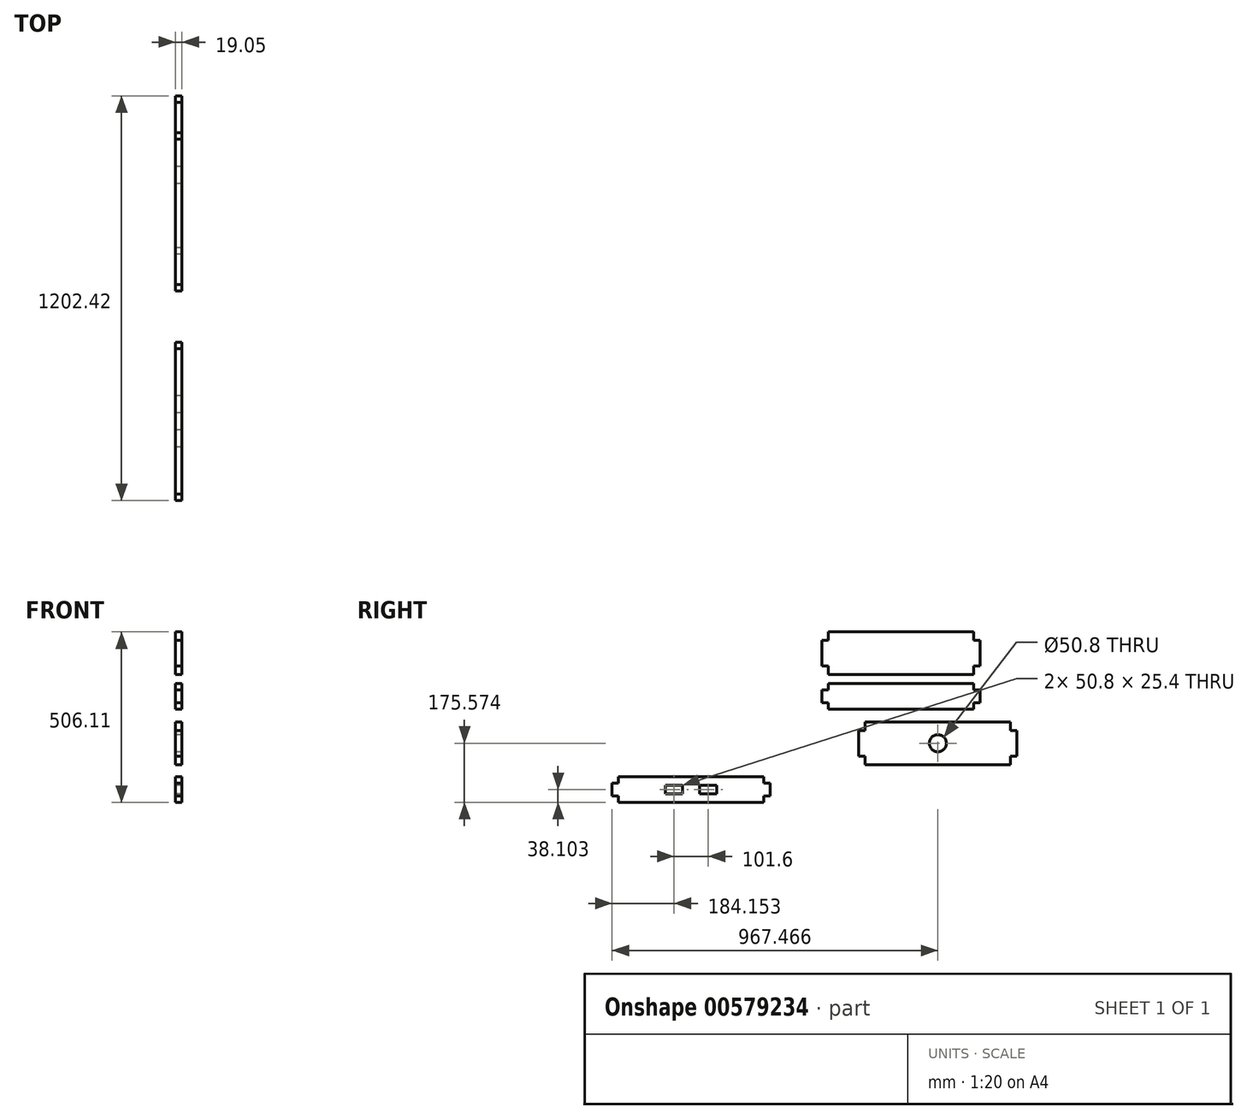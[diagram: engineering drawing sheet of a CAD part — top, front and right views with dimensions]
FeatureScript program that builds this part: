
annotation { "Feature Type Name" : "Feature", "Feature Type Description" : "" }
export const myFeature = defineFeature(function(context is Context, id is Id, definition is map)
    precondition{}
    {
        {
            var Q0;
            Q0=qCreatedBy(makeId("Right.planeOp"),FACE);
            var sketch = newSketch(context, id + "F0", { "sketchPlane" : qUnion([Q0])});
            skLineSegment(sketch, "E0.bottom", {"start": v(-63.54, 0) * mm, "end": v(368.26, 0) * mm});
            skLineSegment(sketch, "E0.top", {"start": v(-63.54, 76.2) * mm, "end": v(368.26, 76.2) * mm});
            skLineSegment(sketch, "E0.left", {"start": v(-63.54, 0) * mm, "end": v(-63.54, 19.05) * mm});
            skLineSegment(sketch, "E0.right", {"start": v(368.26, 0) * mm, "end": v(368.26, 19.05) * mm});
            skLineSegment(sketch, "E1.bottom", {"start": v(-63.54, 57.15) * mm, "end": v(-82.6, 57.15) * mm});
            skLineSegment(sketch, "E1.top", {"start": v(-63.54, 19.05) * mm, "end": v(-82.6, 19.05) * mm});
            skLineSegment(sketch, "E1.right", {"start": v(-82.6, 57.15) * mm, "end": v(-82.6, 19.05) * mm});
            skLineSegment(sketch, "E2.bottom", {"start": v(387.3, 57.15) * mm, "end": v(368.26, 57.15) * mm});
            skLineSegment(sketch, "E2.top", {"start": v(387.3, 19.05) * mm, "end": v(368.26, 19.05) * mm});
            skLineSegment(sketch, "E2.left", {"start": v(387.3, 57.15) * mm, "end": v(387.3, 19.05) * mm});
            skLineSegment(sketch, "E3.trimOffspring", {"start": v(-63.54, 57.15) * mm, "end": v(-63.54, 76.2) * mm});
            skLineSegment(sketch, "E4.trimOffspring", {"start": v(368.26, 57.15) * mm, "end": v(368.26, 76.2) * mm});
            skLineSegment(sketch, "E5.bottom", {"start": v(368.26, 102.68) * mm, "end": v(-63.54, 102.68) * mm});
            skLineSegment(sketch, "E5.top", {"start": v(368.26, 229.68) * mm, "end": v(-63.54, 229.68) * mm});
            skLineSegment(sketch, "E5.left", {"start": v(368.26, 102.68) * mm, "end": v(368.26, 128.08) * mm});
            skLineSegment(sketch, "E5.right", {"start": v(-63.54, 102.68) * mm, "end": v(-63.54, 128.08) * mm});
            skLineSegment(sketch, "E6", {"start": v(368.26, 229.68) * mm, "end": v(368.26, 204.28) * mm});
            skLineSegment(sketch, "E7", {"start": v(387.3, 204.28) * mm, "end": v(368.26, 204.28) * mm});
            skLineSegment(sketch, "E8", {"start": v(387.3, 204.28) * mm, "end": v(387.3, 128.08) * mm});
            skLineSegment(sketch, "E9", {"start": v(368.26, 128.08) * mm, "end": v(387.3, 128.08) * mm});
            skLineSegment(sketch, "E10", {"start": v(-63.54, 229.68) * mm, "end": v(-63.54, 204.28) * mm});
            skLineSegment(sketch, "E11", {"start": v(-63.54, 204.28) * mm, "end": v(-82.6, 204.28) * mm});
            skLineSegment(sketch, "E12", {"start": v(-82.6, 128.08) * mm, "end": v(-82.6, 204.28) * mm});
            skLineSegment(sketch, "E13", {"start": v(-82.6, 128.08) * mm, "end": v(-63.54, 128.08) * mm});
            skLineSegment(sketch, "E14.trimOffspring", {"start": v(-63.54, 204.28) * mm, "end": v(-63.54, 229.68) * mm});
            skLineSegment(sketch, "E15.trimOffspring", {"start": v(368.26, 204.28) * mm, "end": v(368.26, 229.68) * mm});
            skLineSegment(sketch, "E16.bottom", {"start": v(477.67, -164.36) * mm, "end": v(45.87, -164.36) * mm});
            skLineSegment(sketch, "E16.top", {"start": v(477.67, -37.36) * mm, "end": v(45.87, -37.36) * mm});
            skLineSegment(sketch, "E16.left", {"start": v(477.67, -164.36) * mm, "end": v(477.67, -138.96) * mm});
            skLineSegment(sketch, "E16.right", {"start": v(45.87, -164.36) * mm, "end": v(45.87, -138.96) * mm});
            skLineSegment(sketch, "E17", {"start": v(477.67, -37.36) * mm, "end": v(477.67, -62.76) * mm});
            skLineSegment(sketch, "E18", {"start": v(496.72, -62.76) * mm, "end": v(477.67, -62.76) * mm});
            skLineSegment(sketch, "E19", {"start": v(496.72, -62.76) * mm, "end": v(496.72, -138.96) * mm});
            skLineSegment(sketch, "E20", {"start": v(477.67, -138.96) * mm, "end": v(496.72, -138.96) * mm});
            skLineSegment(sketch, "E21", {"start": v(45.87, -37.36) * mm, "end": v(45.87, -62.76) * mm});
            skLineSegment(sketch, "E22", {"start": v(45.87, -62.76) * mm, "end": v(26.82, -62.76) * mm});
            skLineSegment(sketch, "E23", {"start": v(26.82, -138.96) * mm, "end": v(26.82, -62.76) * mm});
            skLineSegment(sketch, "E24", {"start": v(26.82, -138.96) * mm, "end": v(45.87, -138.96) * mm});
            skLineSegment(sketch, "E25.trimOffspring", {"start": v(45.87, -62.76) * mm, "end": v(45.87, -37.36) * mm});
            skLineSegment(sketch, "E26.trimOffspring", {"start": v(477.67, -62.76) * mm, "end": v(477.67, -37.36) * mm});
            skCircle(sketch, "E27", {"center": v(261.77, -100.86) * mm, "radius": 25.4 * mm});
            skLineSegment(sketch, "E28.bottom", {"start": v(-686.65, -276.43) * mm, "end": v(-254.85, -276.43) * mm});
            skLineSegment(sketch, "E28.top", {"start": v(-686.65, -200.23) * mm, "end": v(-254.85, -200.23) * mm});
            skLineSegment(sketch, "E28.left", {"start": v(-686.65, -276.43) * mm, "end": v(-686.65, -257.38) * mm});
            skLineSegment(sketch, "E28.right", {"start": v(-254.85, -276.43) * mm, "end": v(-254.85, -257.38) * mm});
            skLineSegment(sketch, "E29.bottom", {"start": v(-686.65, -219.28) * mm, "end": v(-705.7, -219.28) * mm});
            skLineSegment(sketch, "E29.top", {"start": v(-686.65, -257.38) * mm, "end": v(-705.7, -257.38) * mm});
            skLineSegment(sketch, "E29.right", {"start": v(-705.7, -219.28) * mm, "end": v(-705.7, -257.38) * mm});
            skLineSegment(sketch, "E30.bottom", {"start": v(-235.8, -219.28) * mm, "end": v(-254.85, -219.28) * mm});
            skLineSegment(sketch, "E30.top", {"start": v(-235.8, -257.38) * mm, "end": v(-254.85, -257.38) * mm});
            skLineSegment(sketch, "E30.left", {"start": v(-235.8, -219.28) * mm, "end": v(-235.8, -257.38) * mm});
            skLineSegment(sketch, "E31.trimOffspring", {"start": v(-686.65, -219.28) * mm, "end": v(-686.65, -200.23) * mm});
            skLineSegment(sketch, "E32.trimOffspring", {"start": v(-254.85, -219.28) * mm, "end": v(-254.85, -200.23) * mm});
            skLineSegment(sketch, "E33.bottom", {"start": v(-445.35, -225.63) * mm, "end": v(-394.55, -225.63) * mm});
            skLineSegment(sketch, "E33.top", {"start": v(-445.35, -251.03) * mm, "end": v(-394.55, -251.03) * mm});
            skLineSegment(sketch, "E33.left", {"start": v(-445.35, -225.63) * mm, "end": v(-445.35, -251.03) * mm});
            skLineSegment(sketch, "E33.right", {"start": v(-394.55, -225.63) * mm, "end": v(-394.55, -251.03) * mm});
            skLineSegment(sketch, "E34.bottom", {"start": v(-546.95, -225.63) * mm, "end": v(-496.15, -225.63) * mm});
            skLineSegment(sketch, "E34.top", {"start": v(-546.95, -251.03) * mm, "end": v(-496.15, -251.03) * mm});
            skLineSegment(sketch, "E34.left", {"start": v(-546.95, -225.63) * mm, "end": v(-546.95, -251.03) * mm});
            skLineSegment(sketch, "E34.right", {"start": v(-496.15, -225.63) * mm, "end": v(-496.15, -251.03) * mm});
            skSolve(sketch);
        }
        {
            var Q0;
            Q0=makeQuery(id+"F0.imprint","IMPRINT",FACE,{"disambiguationData":[TD([[makeQuery(id+"F0.imprint","IMPRINT",EDGE,{"derivedFrom":sQuery(id+"F0.wireOp",EDGE,"E0.bottom")}),1.0]])]});
            extrude(context, id + "F1", {"entities" : qUnion([Q0]), "depth" : 19.05 * mm, "offsetDistance" : 25.4 * mm});
        }
        {
            var Q0;
            Q0 = qSketchRegion(id + "F0", true);
            extrude(context, id + "F2", {"entities" : qUnion([Q0]), "operationType" : NewBodyOperationType.ADD, "depth" : 19.05 * mm, "offsetDistance" : 25.4 * mm});
        }
    });
